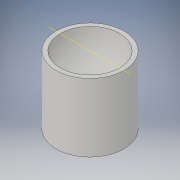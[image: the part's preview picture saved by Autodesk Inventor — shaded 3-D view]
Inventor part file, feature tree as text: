
AUTODESK INVENTOR PART (.ipt)
format: ipt  version: 2017 SP1 (Build 210196100, 196)  size: 114,176 bytes
history: native  units: in
note: dims shown in document units (in); Inventor stores cm internally (conversion verified against a paired STEP export)
features: sketch x2, extrude x1, revolve x1
ambient origin geometry x8: Origin, YZ Plane, XZ Plane, XY Plane, X Axis, Y Axis, Z Axis, Center Point
bodies: Solid1 (feature_tree)
feature tree (4):
  extrude  "Extrusion1"  Depth=4.0in TaperAngle=0.0deg
  revolve  "Revolution1"  Angle=180.0deg
  sketch  "Sketch1"  dims[d0=4.0in d1=4.0in d2=0.0in]
  sketch  "Sketch3"  dims[d4=3.5in d5=180.0deg]
